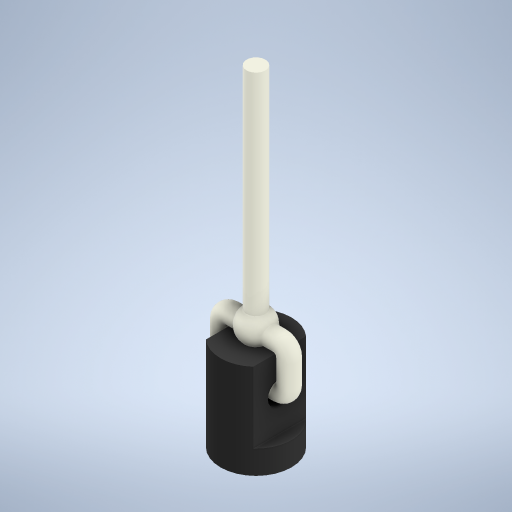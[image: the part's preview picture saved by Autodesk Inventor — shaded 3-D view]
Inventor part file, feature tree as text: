
AUTODESK INVENTOR PART (.ipt)
format: ipt  version: 2024.3 (Build 283343000, 343)  size: 345,600 bytes
history: native  units: mm
features: sketch x7, extrude x4, other x1, sweep x1, plane x1, revolve x1, projected_geometry x1
ambient origin geometry x8: Origin, YZ Plane, XZ Plane, XY Plane, X Axis, Y Axis, Z Axis, Center Point
bodies: Body1 (feature_tree)
feature tree (16):
  other  "솔리드1"
  extrude  "돌출1"  Depth=1.0mm TaperAngle=0.0deg
  extrude  "돌출5"  Depth=2.0mm
  extrude  "돌출6"  Depth=1.0mm
  extrude  "Extrusion7"  Depth=0.4mm TaperAngle=0.0deg
  sweep  "Sweep1"
  plane  "Work Plane2"
  revolve  "Revolution2"  [1 undecoded]
  sketch  "스케치2"
  sketch  "스케치4"
  sketch  "스케치6"
  sketch  "Sketch7"  dims[d0=3.0mm d1=1.0mm d2=0.0mm]
  sketch  "Sketch8"  dims[d6=1.8mm d7=2.0mm]
  sketch  "Sketch9"  dims[d20=3.0mm d21=0.0mm d22=1.0mm]
  projected_geometry  "Projected Loop2"
  sketch  "Sketch11"  dims[d23=1.5mm d24=3.0mm d25=0.0mm d26=0.8mm d27=10.0mm d28=0.0mm d29=0.4mm d30=1.4mm d32=0.4mm d33=0.4mm d34=0.78mm d35=0.0mm d36=0.0mm d39=0.5mm d40=1.4mm d41=90.0deg]
note: 1 required parameter value undecoded (feature->parameter linkage not recoverable at this tier; creation-order binding heuristic only, values carry confidence <= 0.55)
